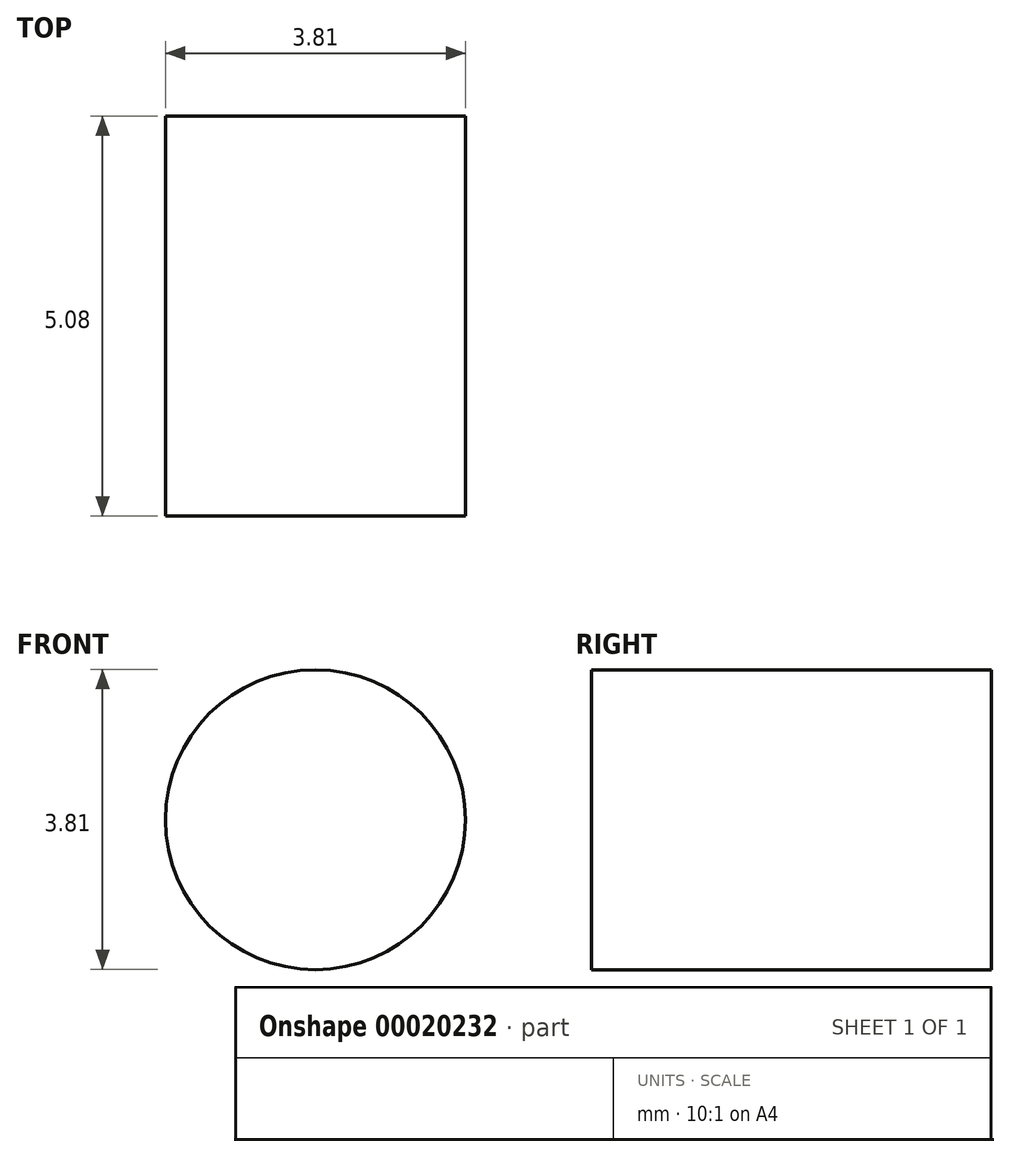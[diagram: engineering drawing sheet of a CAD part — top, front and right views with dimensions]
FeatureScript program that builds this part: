
annotation { "Feature Type Name" : "Feature", "Feature Type Description" : "" }
export const myFeature = defineFeature(function(context is Context, id is Id, definition is map)
    precondition{}
    {
        {
            var Q0;
            Q0=qCreatedBy(makeId("Front.planeOp"),FACE);
            var sketch = newSketch(context, id + "F0", { "sketchPlane" : qUnion([Q0])});
            skCircle(sketch, "E0", {"center": v(-32.52, 34.94) * mm, "radius": 1.9 * mm});
            skSolve(sketch);
        }
        {
            var Q0;
            Q0=makeQuery(id+"F0.imprint","IMPRINT",FACE,{"disambiguationData":[TD([[makeQuery(id+"F0.imprint","IMPRINT",EDGE,{"derivedFrom":sQuery(id+"F0.wireOp",EDGE,"E0")}),1.0]])]});
            extrude(context, id + "F1", {"entities" : qUnion([Q0]), "depth" : 5.08 * mm});
        }
    });
